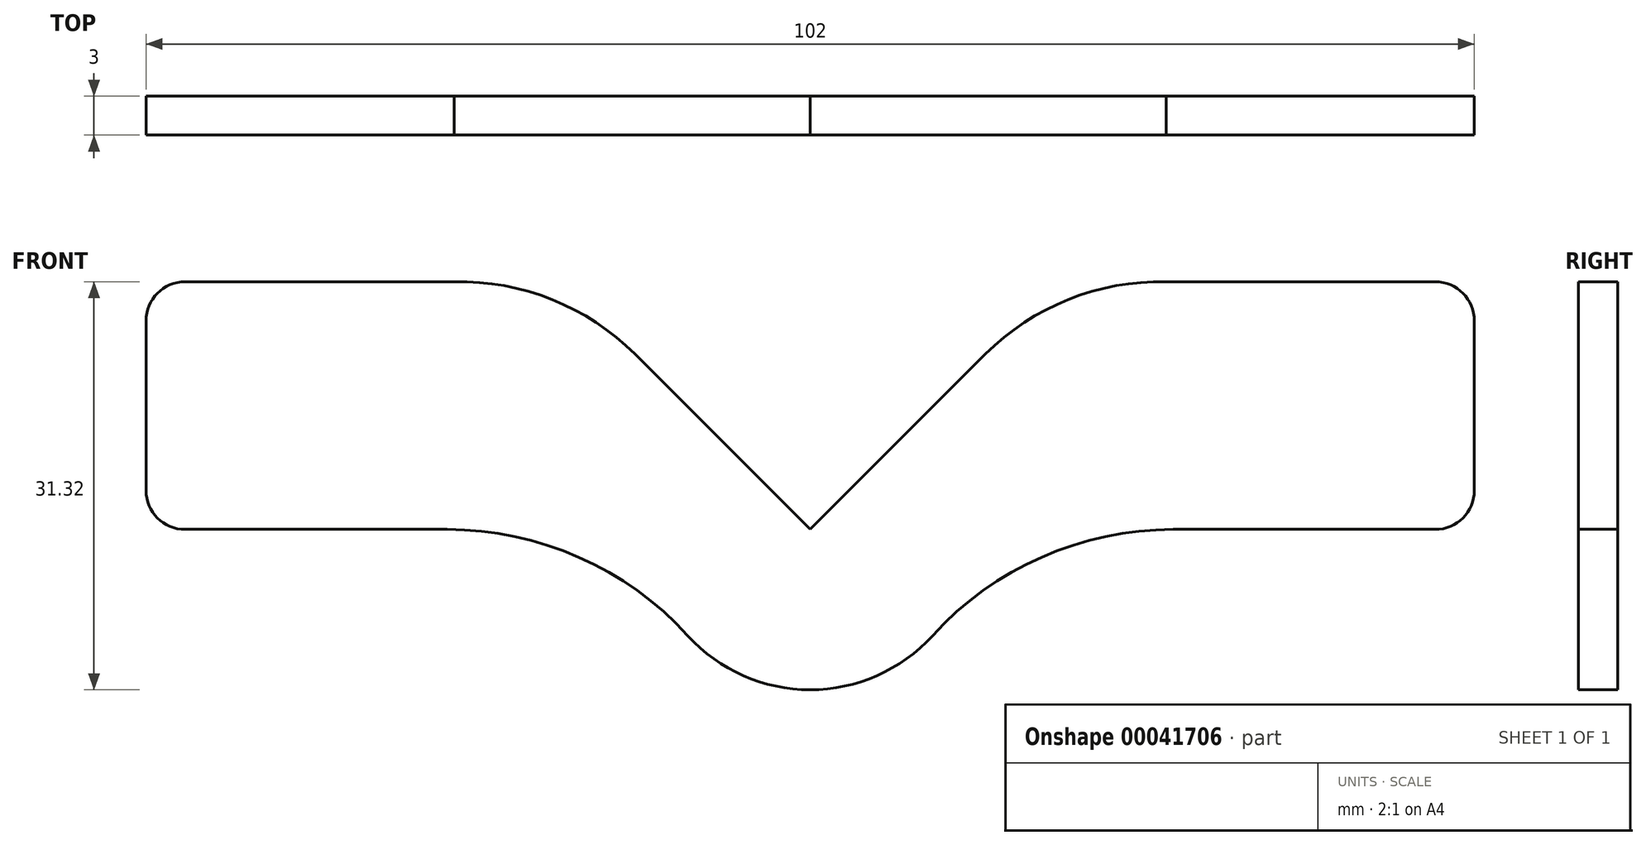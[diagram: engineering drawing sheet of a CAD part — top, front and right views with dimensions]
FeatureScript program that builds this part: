
annotation { "Feature Type Name" : "Feature", "Feature Type Description" : "" }
export const myFeature = defineFeature(function(context is Context, id is Id, definition is map)
    precondition{}
    {
        {
            var Q0;
            Q0=qCreatedBy(makeId("Front.planeOp"),FACE);
            var sketch = newSketch(context, id + "F0", { "sketchPlane" : qUnion([Q0])});
            skLineSegment(sketch, "E0", {"start": v(-51, -25.5) * mm, "end": v(-51, -38.5) * mm});
            skLineSegment(sketch, "E1", {"start": v(-48, -22.5) * mm, "end": v(-27.34, -22.5) * mm});
            skLineSegment(sketch, "E2", {"start": v(-13.44, -28.06) * mm, "end": v(0, -41.5) * mm});
            skLineSegment(sketch, "E3", {"start": v(-48, -41.5) * mm, "end": v(-27.87, -41.5) * mm});
            skLineSegment(sketch, "E4", {"start": v(-27.87, -41.5) * mm, "end": v(0, -41.5) * mm, "construction": true});
            skArc(sketch, "E5", {"start": v(-9.39, -49.66) * mm, "mid": v(-17.77, -43.63) * mm, "end": v(-27.87, -41.5) * mm});
            skLineSegment(sketch, "E6", {"start": v(-9.39, -49.66) * mm, "end": v(-9.39, -49.66) * mm});
            skArc(sketch, "E7.MirrorCS", {"start": v(13.44, -28.06) * mm, "mid": v(19.82, -23.85) * mm, "end": v(27.34, -22.5) * mm});
            skLineSegment(sketch, "E8.MirrorCS", {"start": v(13.44, -28.06) * mm, "end": v(0, -41.5) * mm});
            skLineSegment(sketch, "E9.MirrorCS", {"start": v(48, -22.5) * mm, "end": v(27.34, -22.5) * mm});
            skLineSegment(sketch, "E10.MirrorCS", {"start": v(48, -41.5) * mm, "end": v(27.87, -41.5) * mm});
            skLineSegment(sketch, "E11.MirrorCS", {"start": v(9.39, -49.66) * mm, "end": v(9.39, -49.66) * mm});
            skLineSegment(sketch, "E12.MirrorCS", {"start": v(51, -25.5) * mm, "end": v(51, -38.5) * mm});
            skArc(sketch, "E13.MirrorCS", {"start": v(9.39, -49.66) * mm, "mid": v(17.77, -43.63) * mm, "end": v(27.87, -41.5) * mm});
            skLineSegment(sketch, "E14.MirrorCS", {"start": v(27.87, -41.5) * mm, "end": v(0, -41.5) * mm});
            skArc(sketch, "E15.filletArc", {"start": v(-9.39, -49.66) * mm, "mid": v(0, -53.81) * mm, "end": v(9.39, -49.66) * mm});
            skArc(sketch, "E16.trimOffspring", {"start": v(-13.44, -28.06) * mm, "mid": v(-19.82, -23.85) * mm, "end": v(-27.34, -22.5) * mm});
            skPoint(sketch, "E17.center.orphan", {"position": v(-26.87, -41.5) * mm});
            skArc(sketch, "E18.filletArc", {"start": v(-48, -22.5) * mm, "mid": v(-50.12, -23.38) * mm, "end": v(-51, -25.5) * mm});
            skPoint(sketch, "E19.visualSharp", {"position": v(-51, -41.5) * mm});
            skArc(sketch, "E19.filletArc", {"start": v(-51, -38.5) * mm, "mid": v(-50.12, -40.62) * mm, "end": v(-48, -41.5) * mm});
            skArc(sketch, "E20.filletArc", {"start": v(51, -25.5) * mm, "mid": v(50.12, -23.38) * mm, "end": v(48, -22.5) * mm});
            skPoint(sketch, "E21.visualSharp", {"position": v(51, -41.5) * mm});
            skArc(sketch, "E21.filletArc", {"start": v(48, -41.5) * mm, "mid": v(50.12, -40.62) * mm, "end": v(51, -38.5) * mm});
            skSolve(sketch);
        }
        {
            var Q0;
            Q0 = qSketchRegion(id + "F0", true);
            extrude(context, id + "F1", {"entities" : qUnion([Q0]), "depth" : 3 * mm});
        }
    });
